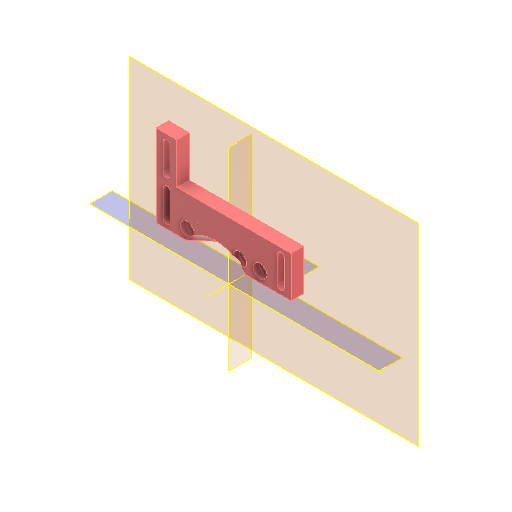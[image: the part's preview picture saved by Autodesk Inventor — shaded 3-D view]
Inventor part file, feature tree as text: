
AUTODESK INVENTOR PART (.ipt)
format: ipt  version: 2022 (Build 260153000, 153)  size: 260,096 bytes
history: native  units: mm
features: other x12, reference x10, plane x8, sketch x5, extrude x4, projected_geometry x2, hole x1, revolve x1
ambient origin geometry x8: Origin, YZ Plane, XZ Plane, XY Plane, X Axis, Y Axis, Z Axis, Center Point
bodies: Volumenkörper1 (feature_tree)
feature tree (43):
  plane  "Arbeitsebene1"
  plane  "Arbeitsebene2"
  extrude  "Extrusion1"  Depth=38.0mm
  hole  "Bohrung1"  [1 undecoded]
  sketch  "Skizze3"  dims[d2=2.9mm d3=6.0mm d4=6.5mm d5=3.0mm d6=90.0deg d7=8.0mm d8=20.594885mm d9=38.0mm]
  other  "Arbeitspunkt1"
  plane  "Arbeitsebene4"
  plane  "Arbeitsebene5"
  extrude  "Extrusion2"  Depth=10.0mm
  plane  "Arbeitsebene3"
  other  "Arbeitsachse1"
  revolve  "Umdrehung1"
  plane  "Arbeitsebene8"
  extrude  "Extrusion5"  Depth=10.0mm
  extrude  "Extrusion6"  Depth=10.0mm
  reference  "Referenz1"
  reference  "Referenz3"
  reference  "Referenz4"
  sketch  "Skizze2"  dims[d0=10.0mm d1=0.0mm]
  reference  "Referenz5"
  reference  "Referenz6"
  reference  "Referenz7"
  projected_geometry  "Projizierte Kontur1"
  reference  "Referenz8"
  reference  "Referenz9"
  plane  "Arbeitsebene6"
  plane  "Arbeitsebene7"
  sketch  "Skizze7"  dims[d10=10.0mm d11=10.0mm]
  reference  "Referenz17"
  sketch  "Skizze8"  dims[d12=10.0mm d13=10.0mm]
  reference  "Referenz18"
  sketch  "Skizze9"  dims[d14=6.0mm d15=0.0mm d30=10.0mm d31=10.0mm d32=10.0mm d33=10.0mm d34=6.5mm d35=3.2mm d36=6.5mm d37=3.2mm d47=11.8mm d49=20.0mm d50=6.5mm d51=3.2mm d52=25.0mm d53=90.0deg d54=0.1mm d55=12.5mm d56=0.0mm d57=5.0mm d58=0.0mm d59=0.0mm]
  projected_geometry  "Projizierte Kontur3"
  other  "Assemlby_Scanner_v1.iam"
  other  "00_CCTV_lens_M12_25mm_5mp:1"
  other  "Assemlby_lightsheet_generator_passive_v2.iam"
  other  "30_Lightsheet_generator_passive_lid_v0:1"
  other  "Assembly_Guinardia_V4.iam"
  other  "10_Wellplate_base_v3:1"
  other  "00_Thorlabs_LJ1878L1-A-Step:1"
  other  "30_Scanlens_Laseradaper_v1:1"
  other  "Assembly_Guinardia_V2.iam"
  other  "10_Wellplate_base_v2:1"
note: 1 required parameter value undecoded (feature->parameter linkage not recoverable at this tier; creation-order binding heuristic only, values carry confidence <= 0.55)
